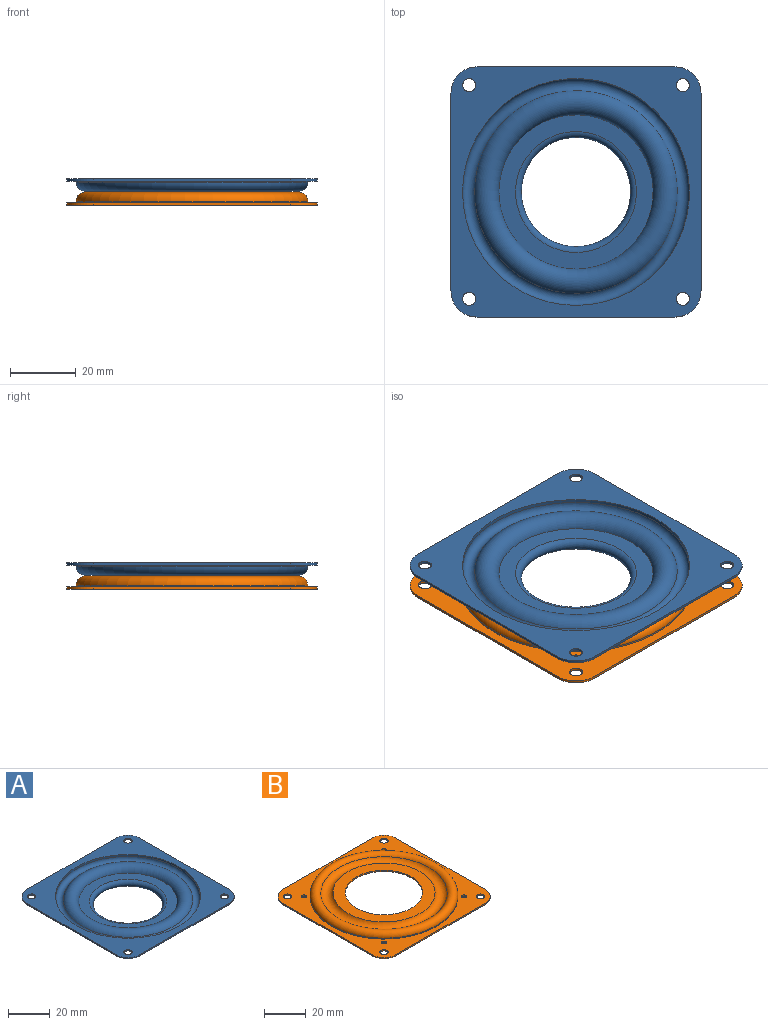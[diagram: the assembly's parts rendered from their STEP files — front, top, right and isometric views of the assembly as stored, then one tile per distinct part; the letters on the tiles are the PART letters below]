
ASSEMBLY  parts=2 mates=1
PART A: 27 faces, bbox 76.4x76.4x6.6 mm
  f0: torus R=18.41mm, axis (0,0,-1), area 364.9mm2, adj f16,f17
  f1: cylinder r=1.98mm len=3.97mm, axis (0,0,-1), area 9.2mm2, adj f14,f15
  f2: cylinder r=1.98mm len=3.97mm, axis (0,0,-1), area 9.2mm2, adj f14,f15
  f3: cylinder r=1.98mm len=3.97mm, axis (0,0,-1), area 9.2mm2, adj f14,f15
  f4: cylinder r=1.98mm len=3.97mm, axis (0,0,-1), area 9.2mm2, adj f14,f15
  f5: cylinder r=7.95mm len=7.95mm, axis (0,0,1), area 9.2mm2, adj f14,f15,f20,f23
  f6: cylinder r=34.56mm len=69.12mm, axis (0,0,-1), area 230.3mm2, adj f7,f14
  f7: torus R=32.57mm, axis (0,0,-1), area 1082.2mm2, adj f6,f8
  f8: torus R=27.37mm, axis (0,0,-1), area 1612.1mm2, adj f7,f19
  f9: torus R=18.41mm, axis (0,0,-1), area 606.6mm2, adj f18,f19
  f10: cylinder r=20.96mm len=41.92mm, axis (0,0,-1), area 97mm2, adj f17,f18
  f11: torus R=27.37mm, axis (0,0,-1), area 1404mm2, adj f12,f16
  f12: torus R=32.57mm, axis (0,0,-1), area 1489.5mm2, adj f11,f13
  f13: cylinder r=35.29mm len=70.59mm, axis (0,0,-1), area 71.8mm2, adj f12,f15
  f14: plane 76.2x76.2mm, normal (0,0,1), area 1950.9mm2, adj f1,f2,f3,f4,f5,f6,f20,f21
  f15: plane 76.2x76.2mm, normal (0,0,-1), area 1789.2mm2, adj f1,f2,f3,f4,f5,f13,f20,f21
  f16: plane 48.27x48.27mm, normal (0,0,-1), area 764.7mm2, adj f0,f11
  f17: plane 41.92x41.92mm, normal (0,0,1), area 314.7mm2, adj f0,f10
  f18: plane 41.92x41.92mm, normal (0,0,-1), area 314.7mm2, adj f9,f10
  f19: plane 47.01x47.01mm, normal (0,0,1), area 670mm2, adj f8,f9
  f20: plane 60.3x0.74mm, normal (-1,0,0), area 44.4mm2, adj f5,f14,f15,f26
  f21: plane 60.3x0.74mm, normal (0,1,0), area 44.4mm2, adj f14,f15,f25,f26
  f22: plane 60.3x0.74mm, normal (1,0,0), area 44.4mm2, adj f14,f15,f24,f25
  f23: plane 60.3x0.74mm, normal (0,-1,0), area 44.4mm2, adj f5,f14,f15,f24
  f24: cylinder r=7.95mm len=7.95mm, axis (0,0,1), area 9.2mm2, adj f14,f15,f22,f23
  f25: cylinder r=7.95mm len=7.95mm, axis (0,0,1), area 9.2mm2, adj f14,f15,f21,f22
  f26: cylinder r=7.95mm len=7.95mm, axis (0,0,1), area 9.2mm2, adj f14,f15,f20,f21
PART B: 27 faces, bbox 76.4x76.4x4.8 mm
  f0: cylinder r=1.19mm len=2.38mm, axis (0,0,-1), area 5.5mm2, adj f15,f16
  f1: cylinder r=1.19mm len=2.38mm, axis (0,0,-1), area 5.5mm2, adj f15,f16
  f2: cylinder r=1.19mm len=2.38mm, axis (0,0,-1), area 5.5mm2, adj f15,f16
  f3: cylinder r=1.19mm len=2.38mm, axis (0,0,-1), area 5.5mm2, adj f15,f16
  f4: cylinder r=1.98mm len=3.97mm, axis (0,0,-1), area 9.2mm2, adj f15,f16
  f5: cylinder r=1.98mm len=3.97mm, axis (0,0,-1), area 9.2mm2, adj f15,f16
  f6: cylinder r=1.98mm len=3.97mm, axis (0,0,-1), area 9.2mm2, adj f15,f16
  f7: cylinder r=1.98mm len=3.97mm, axis (0,0,-1), area 9.2mm2, adj f15,f16
  f8: cylinder r=35.29mm len=70.59mm, axis (0,0,-1), area 111.2mm2, adj f9,f15
  f9: torus R=32.57mm, axis (0,0,-1), area 1489.5mm2, adj f8,f10
  f10: torus R=27.37mm, axis (0,0,-1), area 1253.2mm2, adj f9,f18
  f11: cylinder r=18.41mm len=36.83mm, axis (0,0,-1), area 85.2mm2, adj f17,f18
  f12: torus R=27.37mm, axis (0,0,-1), area 1457.9mm2, adj f13,f17
  f13: torus R=32.57mm, axis (0,0,-1), area 1082.2mm2, adj f12,f14
  f14: cylinder r=34.56mm len=69.12mm, axis (0,0,-1), area 268.9mm2, adj f13,f16
  f15: plane 76.2x76.2mm, normal (0,0,1), area 1771.4mm2, adj f0,f1,f2,f3,f4,f5,f6,f7
  f16: plane 76.2x76.2mm, normal (0,0,-1), area 1933.1mm2, adj f0,f1,f2,f3,f4,f5,f6,f7
  f17: plane 47.75x47.75mm, normal (0,0,-1), area 725.1mm2, adj f11,f12
  f18: plane 48.69x48.69mm, normal (0,0,1), area 796.3mm2, adj f10,f11
  f19: plane 60.3x0.74mm, normal (0,-1,0), area 44.4mm2, adj f15,f16,f23,f24
  f20: plane 60.3x0.74mm, normal (-1,0,0), area 44.4mm2, adj f15,f16,f23,f25
  f21: plane 60.3x0.74mm, normal (0,1,0), area 44.4mm2, adj f15,f16,f25,f26
  f22: plane 60.3x0.74mm, normal (1,0,0), area 44.4mm2, adj f15,f16,f24,f26
  f23: cylinder r=7.95mm len=7.95mm, axis (0,0,-1), area 9.2mm2, adj f15,f16,f19,f20
  f24: cylinder r=7.95mm len=7.95mm, axis (0,0,-1), area 9.2mm2, adj f15,f16,f19,f22
  f25: cylinder r=7.95mm len=7.95mm, axis (0,0,-1), area 9.2mm2, adj f15,f16,f20,f21
  f26: cylinder r=7.95mm len=7.95mm, axis (0,0,-1), area 9.2mm2, adj f15,f16,f21,f22
PLACE A t=(-62.1,-26.29,3.62)mm
PLACE B t=(-62.1,-26.29,3.62)mm
MATE revolute A.f0 <-> B.f8  axis (0,0,1) through (-62.1,-26.29,11.75)mm
